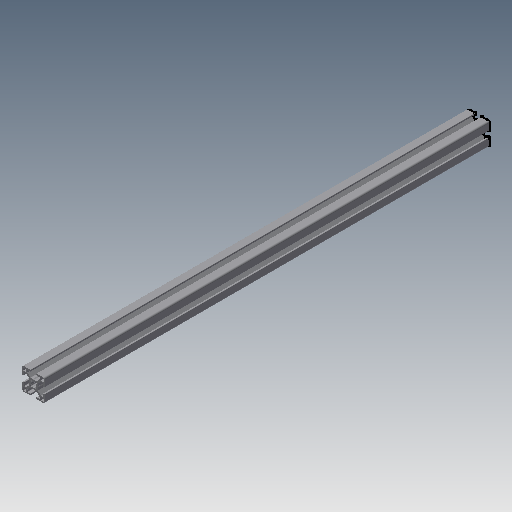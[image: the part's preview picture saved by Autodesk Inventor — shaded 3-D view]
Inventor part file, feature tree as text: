
AUTODESK INVENTOR PART (.ipt)
format: ipt  version: 2017 (Build 210142000, 142)  size: 351,744 bytes
history: native  units: mm
features: sketch x2, extrude x1, plane x1
ambient origin geometry x8: Origin, YZ Plane, XZ Plane, XY Plane, X Axis, Y Axis, Z Axis, Center Point
bodies: Solid1 (feature_tree)
feature tree (4):
  sketch  "Sketch1"  dims[d0=600.0mm d1=0.0mm]
  extrude  "Extrusion1"  [1 undecoded]
  plane  "Work Plane1"
  sketch  "Sketch3"
note: 1 required parameter value undecoded (feature->parameter linkage not recoverable at this tier; creation-order binding heuristic only, values carry confidence <= 0.55)
